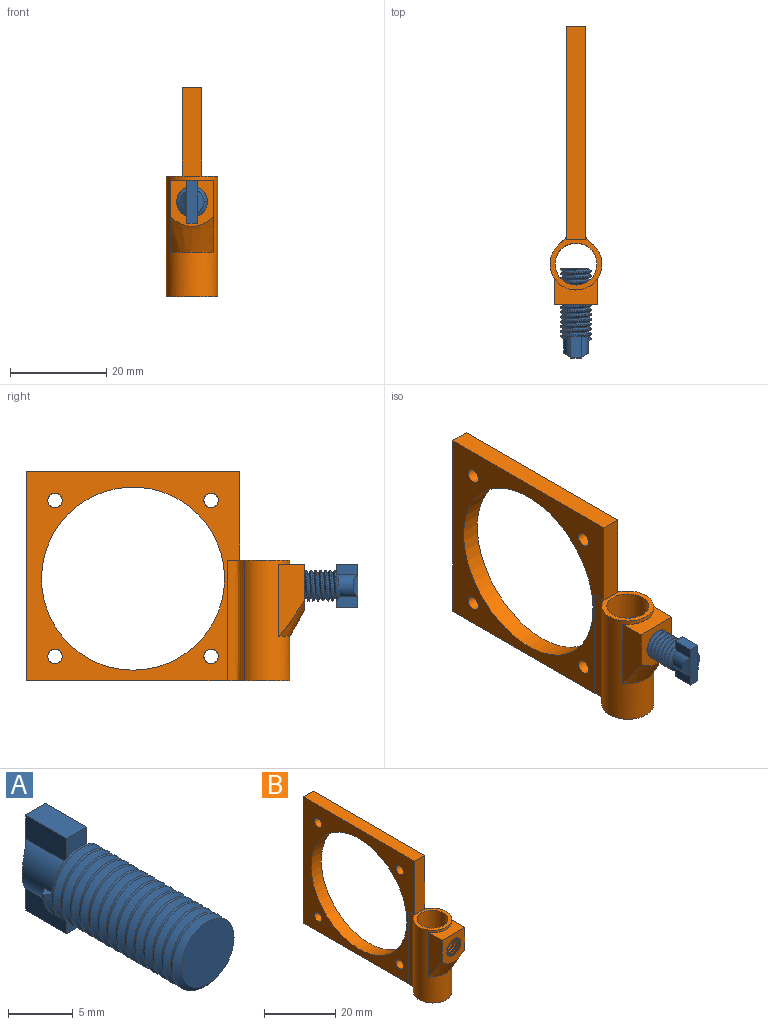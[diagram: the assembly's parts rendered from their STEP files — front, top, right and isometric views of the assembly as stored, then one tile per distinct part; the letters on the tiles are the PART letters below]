
ASSEMBLY  parts=2 mates=1
PART A: 20 faces, bbox 6.4x19.1x9.1 mm
  f0: plane 4.51x2.26mm, normal (-1,0,0), area 10.1mm2, adj f3,f6,f7,f11,f12
  f1: plane 4.52x2.28mm, normal (1,0,0), area 10.1mm2, adj f6,f7,f11,f12,f17
  f2: plane 4.54x2.29mm, normal (-1,0,0), area 9.7mm2, adj f3,f5,f8,f9,f12,f13,f14
  f3: cylinder r=2.5mm len=18.5mm, axis (0,1,0), area 3.1mm2, adj f0,f2,f5,f6,f14,f15,f16,f19
  f4: cylinder r=3.17mm len=14.3mm, axis (0,1,0), area 82.8mm2, adj f5,f6,f10,f16
  f5: bspline ~14.89x7.32mm, area 196.5mm2, adj f2,f3,f4,f8,f10,f13,f15,f16
  f6: bspline ~15.22x7.32mm, area 198.8mm2, adj f0,f1,f3,f4,f7,f10,f16,f17
  f7: plane 2.25x1.96mm, normal (0,-1,0), area 3.6mm2, adj f0,f1,f6,f11
  f8: plane 2.25x1.95mm, normal (0,-1,0), area 3.6mm2, adj f2,f5,f9,f10
  f9: plane 4.5x2.2mm, normal (0,0,-1), area 9.9mm2, adj f2,f8,f10,f12
  f10: plane 4.54x2.29mm, normal (1,0,0), area 9.8mm2, adj f4,f5,f6,f8,f9,f12,f17
  f11: plane 4.5x2.2mm, normal (0,0,1), area 9.9mm2, adj f0,f1,f7,f12
  f12: plane 9x2.2mm, normal (0,1,0), area 19.8mm2, adj f0,f1,f2,f9,f10,f11,f18,f19
  f13: cylinder r=3.17mm len=2.97mm, axis (0,1,0), area 0.9mm2, adj f2,f5,f14,f15
  f14: bspline ~4.76x3.66mm, area 2.6mm2, adj f2,f3,f13,f15
  f15: plane 1x0.67mm, normal (0,0,1), area 0.4mm2, adj f3,f5,f13,f14
  f16: plane 5.9x5.69mm, normal (0,-1,0), area 26.8mm2, adj f3,f4,f5,f6
  f17: cylinder r=2.5mm len=4.49mm, axis (0,-1,0), area 18.4mm2, adj f1,f6,f10,f18
  f18: cylinder r=5mm len=4.49mm, axis (0,0,-1), area 5.7mm2, adj f12,f17
  f19: cylinder r=5mm len=4.49mm, axis (0,0,-1), area 5.7mm2, adj f3,f12
PART B: 23 faces, bbox 20.6x63.6x49.3 mm
  f0: cylinder r=4.35mm len=25mm, axis (0,0,-1), area 658.5mm2, adj f3,f13,f21,f22
  f1: cylinder r=5.39mm len=25mm, axis (0,0,-1), area 486.9mm2, adj f3,f13,f14,f15,f17,f18,f19,f20
  f2: plane 18.4x4mm, normal (0,-1,0), area 73.6mm2, adj f5,f11,f12,f13
  f3: plane 55.88x11.87mm, normal (0,0,-1), area 209mm2, adj f0,f1,f4,f11,f12,f14,f15
  f4: plane 43.4x4mm, normal (0,1,0), area 173.6mm2, adj f3,f5,f11,f12
  f5: plane 44.4x4mm, normal (0,0,1), area 177.6mm2, adj f2,f4,f11,f12
  f6: cylinder r=1.5mm len=4mm, axis (-1,0,0), area 37.7mm2, adj f11,f12
  f7: cylinder r=19mm len=38mm, axis (-1,0,0), area 477.5mm2, adj f11,f12
  f8: cylinder r=1.5mm len=4mm, axis (-1,0,0), area 37.7mm2, adj f11,f12
  f9: cylinder r=1.5mm len=4mm, axis (-1,0,0), area 37.7mm2, adj f11,f12
  f10: cylinder r=1.5mm len=4mm, axis (-1,0,0), area 37.7mm2, adj f11,f12
  f11: plane 44.4x43.4mm, normal (1,0,0), area 697.8mm2, adj f2,f3,f4,f5,f6,f7,f8,f9
  f12: plane 44.4x43.4mm, normal (-1,0,0), area 697.8mm2, adj f2,f3,f4,f5,f6,f7,f8,f9
  f13: plane 14.15x11.87mm, normal (0,0,1), area 31.4mm2, adj f0,f1,f2,f11,f12,f14,f15
  f14: bspline ~27.5x3.69mm, area 109.1mm2, adj f1,f3,f11,f13
  f15: bspline ~27.5x3.69mm, area 109.1mm2, adj f1,f3,f12,f13
  f16: plane 14.26x13.66mm, normal (0,-1,0), area 56.4mm2, adj f17,f18,f19,f20,f21
  f17: plane 16.29x6.72mm, normal (1,0,0), area 62.6mm2, adj f1,f16,f19,f20
  f18: plane 16.29x6.72mm, normal (-1,0,0), area 62.6mm2, adj f1,f16,f19,f20
  f19: plane 9x5.43mm, normal (0,0,1), area 33.5mm2, adj f1,f16,f17,f18
  f20: cone r=5.39mm half-angle=29.1deg, axis (0,0,1), area 91mm2, adj f1,f16,f17,f18
  f21: cylinder r=2.87mm len=5.74mm, axis (0,-1,0), area 37.7mm2, adj f0,f16
  f22: cylinder r=2.87mm len=3.57mm, axis (0,-1,0), area 0mm2, adj f0
PLACE A rot(axis=(0,0,1),180deg) t=(10.98,-16.65,16.76)mm
PLACE B t=(8.98,9.34,18.23)mm
MATE parallel A.f3 <-> B.f16  axis (0,1,0) through (10.98,-2.65,16.76)mm
